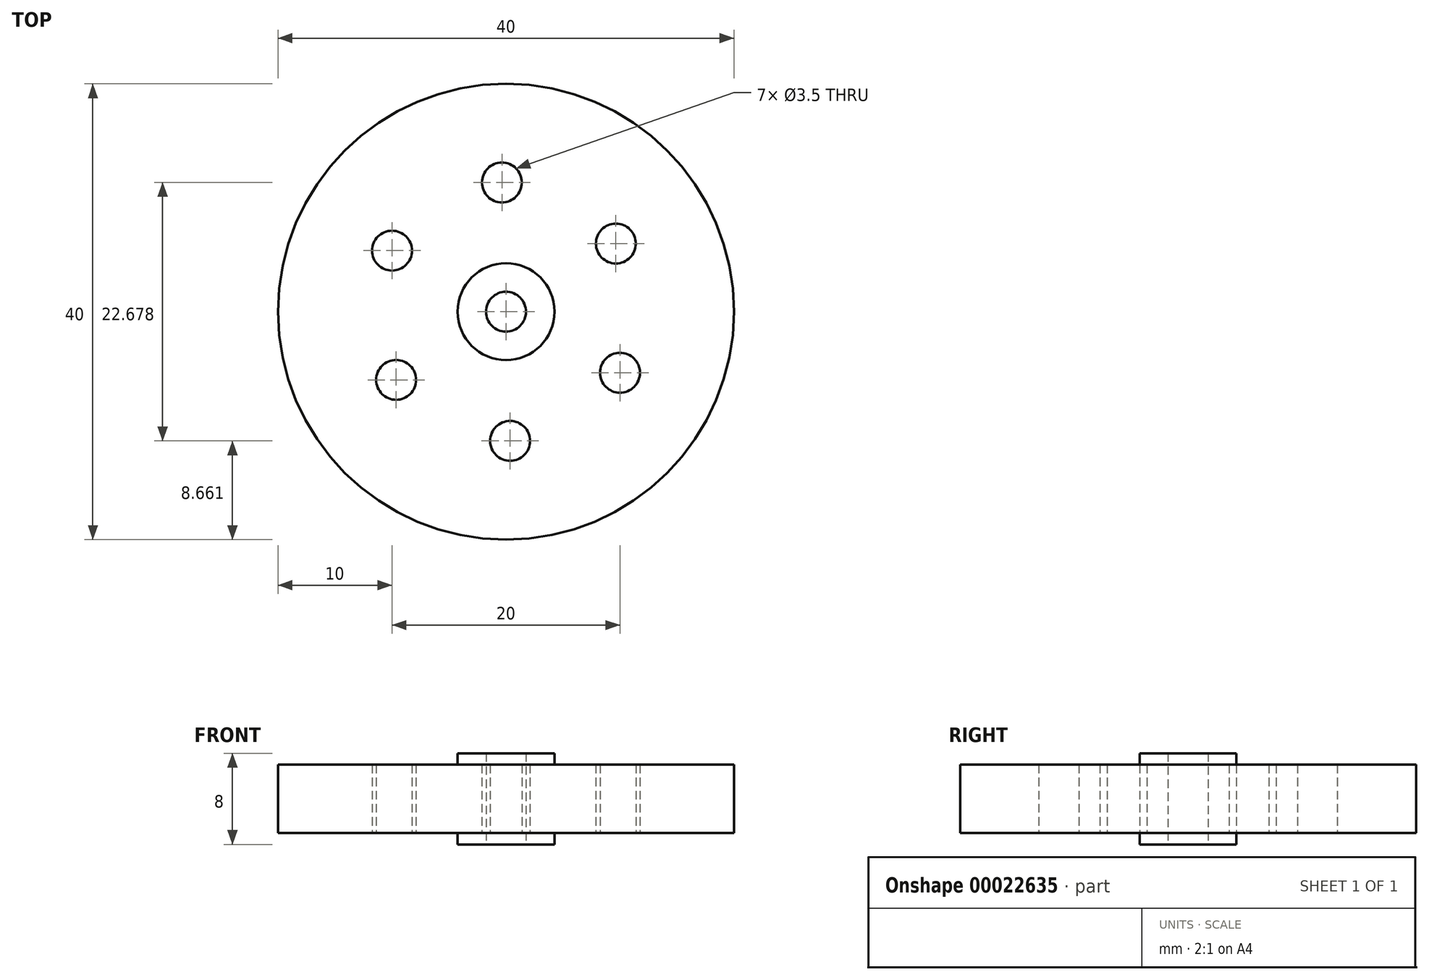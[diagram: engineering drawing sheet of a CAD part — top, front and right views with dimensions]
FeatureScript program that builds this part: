
annotation { "Feature Type Name" : "Feature", "Feature Type Description" : "" }
export const myFeature = defineFeature(function(context is Context, id is Id, definition is map)
    precondition{}
    {
        {
            var Q0;
            Q0=qCreatedBy(makeId("Top.planeOp"),FACE);
            var sketch = newSketch(context, id + "F0", { "sketchPlane" : qUnion([Q0])});
            skCircle(sketch, "E0", {"center": v(0, 0) * mm, "radius": 20 * mm});
            skCircle(sketch, "E1", {"center": v(-10, 5.36) * mm, "radius": 1.75 * mm});
            skCircle(sketch, "E2.1.0", {"center": v(-9.64, -5.98) * mm, "radius": 1.75 * mm});
            skCircle(sketch, "E2.2.0", {"center": v(0.36, -11.34) * mm, "radius": 1.75 * mm});
            skCircle(sketch, "E2.3.0", {"center": v(10, -5.36) * mm, "radius": 1.75 * mm});
            skCircle(sketch, "E2.4.0", {"center": v(9.64, 5.98) * mm, "radius": 1.75 * mm});
            skCircle(sketch, "E2.5.0", {"center": v(-0.36, 11.34) * mm, "radius": 1.75 * mm});
            skCircle(sketch, "E3", {"center": v(0, 0) * mm, "radius": 1.75 * mm});
            skCircle(sketch, "E4", {"center": v(0, 0) * mm, "radius": 4.25 * mm});
            skSolve(sketch);
        }
        {
            var Q0;
            Q0=makeQuery(id+"F0.imprint","IMPRINT",FACE,{"disambiguationData":[TD([[makeQuery(id+"F0.imprint","IMPRINT",EDGE,{"derivedFrom":sQuery(id+"F0.wireOp",EDGE,"E0")}),1.0]])]});
            extrude(context, id + "F1", {"entities" : qUnion([Q0]), "endBound" : BoundingType.SYMMETRIC, "depth" : 6 * mm});
        }
        {
            var Q0;
            Q0=makeQuery(id+"F0.imprint","IMPRINT",FACE,{"disambiguationData":[TD([[makeQuery(id+"F0.imprint","IMPRINT",EDGE,{"derivedFrom":sQuery(id+"F0.wireOp",EDGE,"E3")}),-1.0]])]});
            extrude(context, id + "F2", {"entities" : qUnion([Q0]), "operationType" : NewBodyOperationType.ADD, "endBound" : BoundingType.SYMMETRIC, "depth" : 8 * mm});
        }
    });
